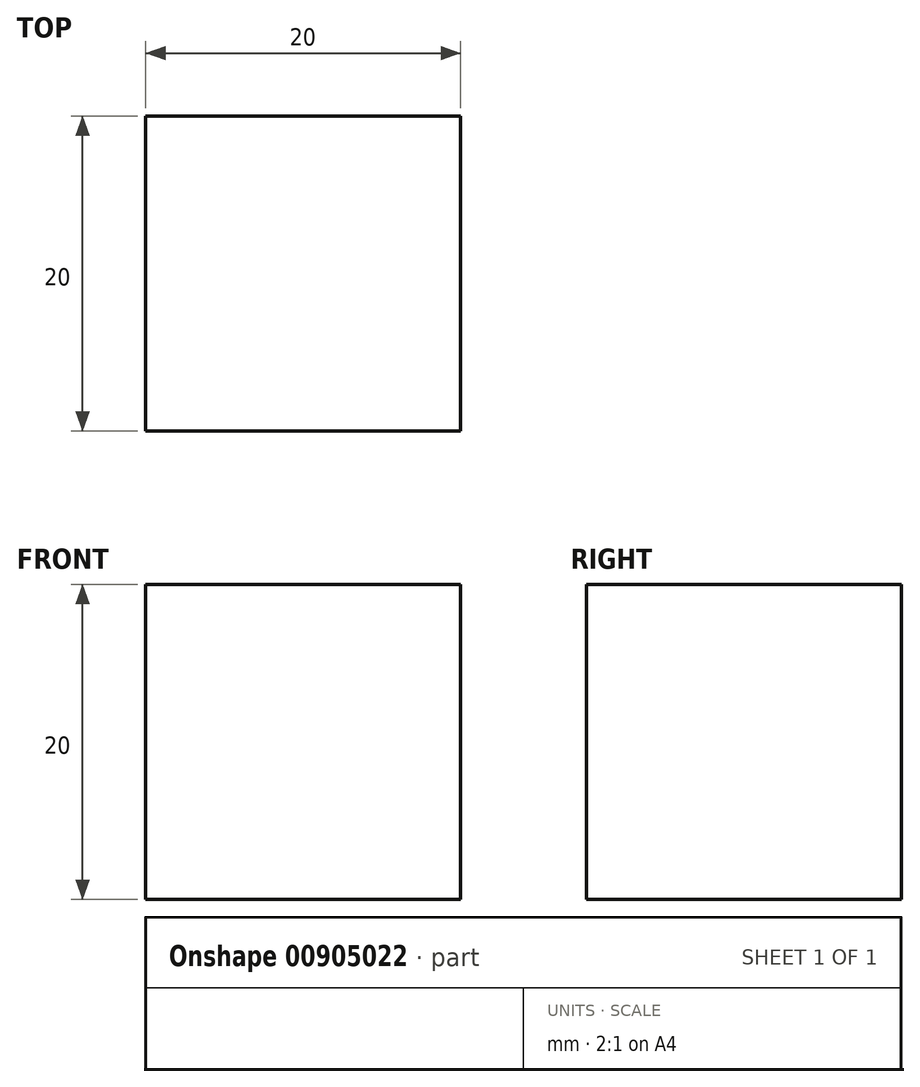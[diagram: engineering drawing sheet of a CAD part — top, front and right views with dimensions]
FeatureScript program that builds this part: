
annotation { "Feature Type Name" : "Feature", "Feature Type Description" : "" }
export const myFeature = defineFeature(function(context is Context, id is Id, definition is map)
    precondition{}
    {
        {
            var Q0;
            Q0=qCreatedBy(makeId("Top.planeOp"),FACE);
            var sketch = newSketch(context, id + "F0", { "sketchPlane" : qUnion([Q0])});
            skLineSegment(sketch, "E0.bottom", {"start": v(-10, 10) * mm, "end": v(10, 10) * mm});
            skLineSegment(sketch, "E0.top", {"start": v(-10, -10) * mm, "end": v(10, -10) * mm});
            skLineSegment(sketch, "E0.left", {"start": v(-10, 10) * mm, "end": v(-10, -10) * mm});
            skLineSegment(sketch, "E0.right", {"start": v(10, 10) * mm, "end": v(10, -10) * mm});
            skPoint(sketch, "E0.middle", {"position": v(0, 0) * mm});
            skSolve(sketch);
        }
        {
            var Q0;
            Q0=makeQuery(id+"F0.imprint","IMPRINT",FACE,{"disambiguationData":[TD([[makeQuery(id+"F0.imprint","IMPRINT",EDGE,{"derivedFrom":sQuery(id+"F0.wireOp",EDGE,"E0.bottom")}),-1.0]])]});
            extrude(context, id + "F1", {"entities" : qUnion([Q0]), "depth" : 20 * mm, "offsetDistance" : 25 * mm});
        }
    });
